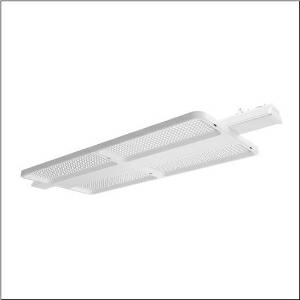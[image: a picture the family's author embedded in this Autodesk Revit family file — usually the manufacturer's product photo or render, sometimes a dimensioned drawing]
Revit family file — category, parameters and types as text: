
# Revit family: highbay_11_fur_licross_r__tragschiene_maxi_51hn11db4qla_d97e
name_source: partatom
category: Lighting Fixtures
units: mm (PartAtom-declared; Revit-internal decimal feet)

## family parameters
Cut with Voids When Loaded = No
Host = Face
Light Source = No
Part Type = Normal
Room Calculation Point = No
Round Connector Dimension = Use Diameter
Shared = No

## types (1)
- --- (1 x LED, 36000 lm, 177.7 W, 4000K)
    Apparent Load = 178 VA
    CIE Flux Codes = 85 97 100 100 100
    Color Rendering = 80
    Color Temperature = 4000K
    Default Elevation = 1800 mm
    Description = Highbay 11 for Licross® trunking rail maxi, high bay luminaire, primary light control with lens, of PMMA, primary optical cover: cover, of PMMA, light emission: direct distribution, primary light characteristic: symmetric, LED, rated luminous flux: 36.000lm, luminous efficacy: 203lm/W, light colour: 840, colour temperature: 4000K, control gear: DALI 2, with plug, 5-pole, with phase selection, mains connection: 230..240V, AC, 50/60Hz, rated input power: 177.7W, housing frame, of high-performance plastic PA6, matt traffic white (RAL 9016), length: 1.250mm, width: 442mm, height: 71mm, lever catch, fixing on rail side, of steel, galvanised, white, blank cover, of PC/ABS, traffic white (RAL 9016), protection rating (complete): IP64, insulation class (complete): insulation class I (protective earthing), certification: CE, ENEC, VDE, UKCA, protection symbol: D, impact resistance: IK07, permissible operating ambient temperature: -40..+55°C, corresponds to IFS (International Featured Standards) requirements for safety and quality in the food industry, LABS conformity tested according to VDMA 24364:2018-05, packaging unit: 1 piece
    Height = 72 mm  [stored 0.23622 ft]
    Lamp = 1 x LED
    Lamp Light Flux = 36000 lm
    Lamp Power = 177.7 W
    Lamp count = 1
    Length = 946 mm
    Luminous efficacy = 203 lm/W
    Manufacturer = Siteco
    ModVariant = No
    Model = 51HN11DB4QLA
    Mounting Place = Ceiling
    Mounting Type = Pendant
    Number of Poles = 1
    OnlyDefault = Yes
    Power Factor = 1
    Product Name = Highbay 11 für Licross® Tragschiene maxi
    Product group = high bay luminaire
    ProductGroupID = 901
    Protection Class = Protection class I
    Protection Degree = IP 64
    RLX_Detail_Level = 1
    RLX_Emergency_Light_Flux = 0 lm
    RLX_Emergency_Type = 0
    RLX_Emergency_Type_DB = No
    RlxData = <blob elided: 24077 chars, md5=47ffb293>
    Socket = socket
    Standby Power = 0 W
    System Light Flux = 36000 lm
    System Power = 178 W
    Type Comments = factory setting: luminous flux: 100 % | dim-lin: 254 | 824 mA
    Type Image = l_1361711.jpg
    URL = http://relux.com
    VarID = @adj_004907
    Voltage = 0 V
    Weight = 0.00 kg
    Width = 442 mm

note: [stored X ft] marks values corroborated as IEEE doubles in the binary element streams (Revit-internal decimal feet)

## geometry (parser evidence)
native form markers: Blend x4, Sweep x10
no freeform markers — native parametric forms only
